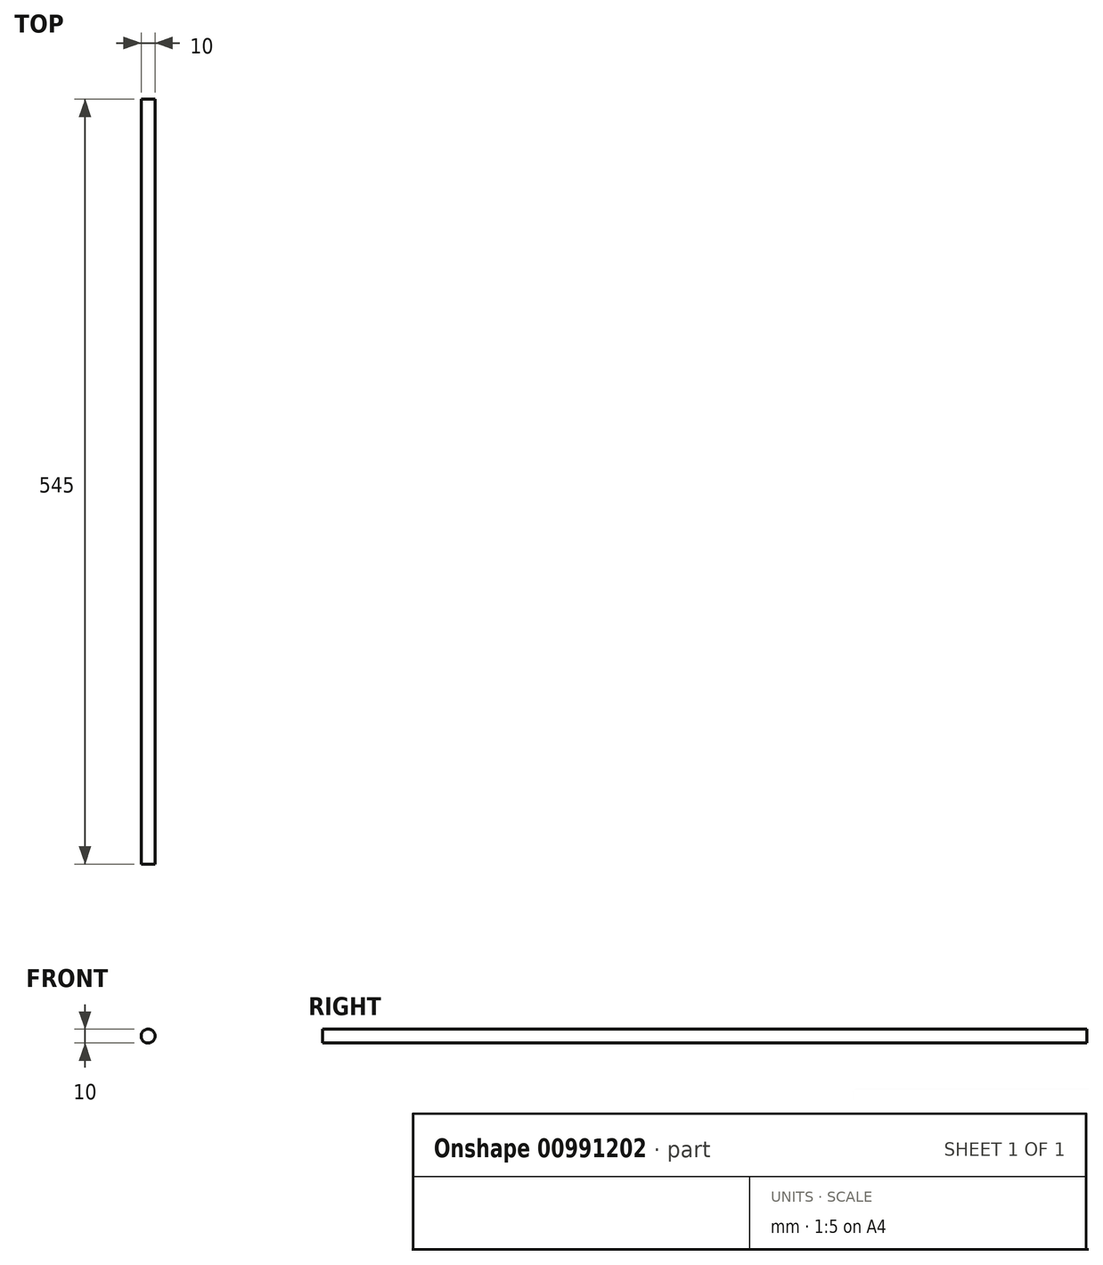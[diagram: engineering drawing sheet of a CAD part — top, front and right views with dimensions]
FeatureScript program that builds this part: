
annotation { "Feature Type Name" : "Feature", "Feature Type Description" : "" }
export const myFeature = defineFeature(function(context is Context, id is Id, definition is map)
    precondition{}
    {
        {
            var Q0;
            Q0=qCreatedBy(makeId("Front.planeOp"),FACE);
            var sketch = newSketch(context, id + "F0", { "sketchPlane" : qUnion([Q0])});
            skCircle(sketch, "E0", {"center": v(0, 0) * mm, "radius": 5 * mm});
            skSolve(sketch);
        }
        {
            var Q0;
            Q0=makeQuery(id+"F0.imprint","IMPRINT",FACE,{"disambiguationData":[TD([[makeQuery(id+"F0.imprint","IMPRINT",EDGE,{"derivedFrom":sQuery(id+"F0.wireOp",EDGE,"E0")}),1.0]])]});
            extrude(context, id + "F1", {"entities" : qUnion([Q0]), "depth" : 545 * mm, "offsetDistance" : 25 * mm, "symmetric" : true});
        }
    });
